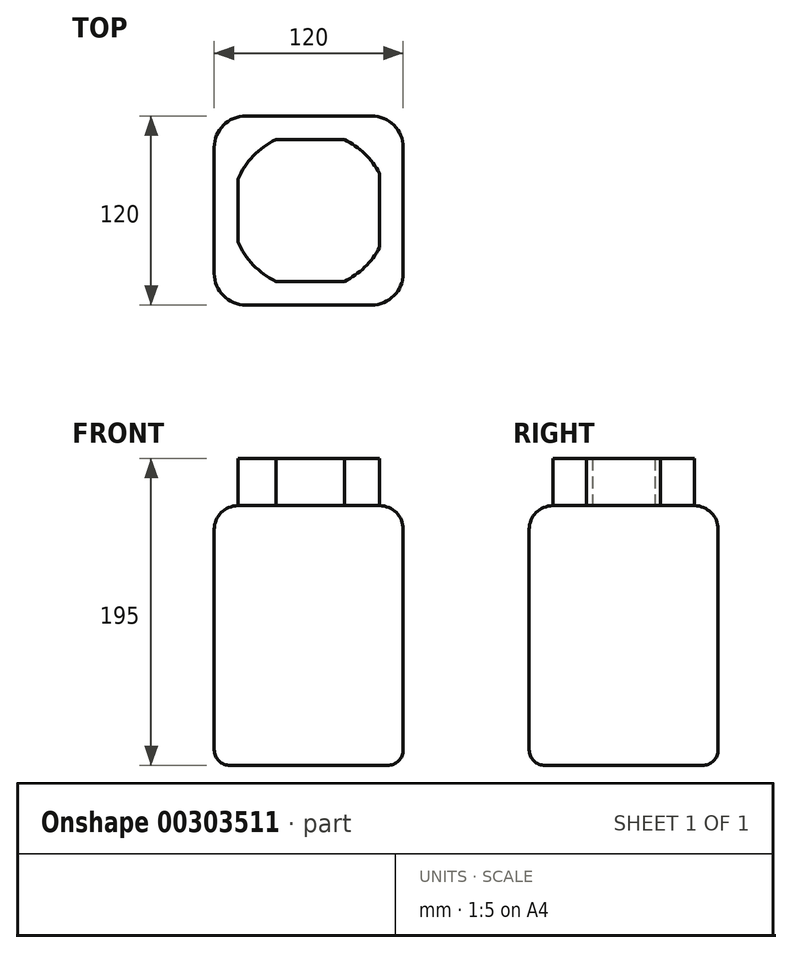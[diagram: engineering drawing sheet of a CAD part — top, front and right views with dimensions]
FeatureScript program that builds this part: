
annotation { "Feature Type Name" : "Feature", "Feature Type Description" : "" }
export const myFeature = defineFeature(function(context is Context, id is Id, definition is map)
    precondition{}
    {
        {
            var Q0;
            Q0=qCreatedBy(makeId("Top.planeOp"),FACE);
            var sketch = newSketch(context, id + "F0", { "sketchPlane" : qUnion([Q0])});
            skLineSegment(sketch, "E0.bottom", {"start": v(-100, 60) * mm, "end": v(-20, 60) * mm});
            skLineSegment(sketch, "E0.top", {"start": v(-100, -60) * mm, "end": v(-20, -60) * mm});
            skLineSegment(sketch, "E0.left", {"start": v(-120, 40) * mm, "end": v(-120, -40) * mm});
            skLineSegment(sketch, "E0.right", {"start": v(0, 40) * mm, "end": v(0, -40) * mm});
            skPoint(sketch, "E1.visualSharp", {"position": v(0, 60) * mm});
            skArc(sketch, "E1.filletArc", {"start": v(0, 40) * mm, "mid": v(-5.86, 54.14) * mm, "end": v(-20, 60) * mm});
            skPoint(sketch, "E2.visualSharp", {"position": v(0, -60) * mm});
            skArc(sketch, "E2.filletArc", {"start": v(-20, -60) * mm, "mid": v(-5.86, -54.14) * mm, "end": v(0, -40) * mm});
            skPoint(sketch, "E3.visualSharp", {"position": v(-120, -60) * mm});
            skArc(sketch, "E3.filletArc", {"start": v(-120, -40) * mm, "mid": v(-114.14, -54.14) * mm, "end": v(-100, -60) * mm});
            skPoint(sketch, "E4.visualSharp", {"position": v(-120, 60) * mm});
            skArc(sketch, "E4.filletArc", {"start": v(-100, 60) * mm, "mid": v(-114.14, 54.14) * mm, "end": v(-120, 40) * mm});
            skSolve(sketch);
        }
        {
            var Q0;
            Q0=makeQuery(id+"F0.imprint","IMPRINT",FACE,{"disambiguationData":[TD([[makeQuery(id+"F0.imprint","IMPRINT",EDGE,{"derivedFrom":sQuery(id+"F0.wireOp",EDGE,"E0.bottom")}),-1.0]])]});
            extrude(context, id + "F1", {"entities" : qUnion([Q0]), "depth" : 165 * mm});
        }
        {
            var Q0;
            Q0=makeQuery(id+"F1.opExtrude","CAP_EDGE",EDGE,{"disambiguationData":[OSD([sQuery(id+"F0.wireOp",EDGE,"E0.top")])],"isStart":true});
            var Q1;
            Q1=makeQuery(id+"F1.opExtrude","CAP_EDGE",EDGE,{"disambiguationData":[OSD([sQuery(id+"F0.wireOp",EDGE,"E3.filletArc")])],"isStart":true});
            var Q2;
            Q2=makeQuery(id+"F1.opExtrude","CAP_EDGE",EDGE,{"disambiguationData":[OSD([sQuery(id+"F0.wireOp",EDGE,"E2.filletArc")])],"isStart":true});
            fillet(context, id + "F2", {"entities" : qUnion([Q0, Q1, Q2]), "radius" : 10 * mm, "tangentPropagation" : true, "allowEdgeOverflow" : false});
        }
        {
            var Q0;
            Q0=makeQuery(id+"F1.opExtrude","CAP_EDGE",EDGE,{"disambiguationData":[OSD([sQuery(id+"F0.wireOp",EDGE,"E0.bottom")])],"isStart":false});
            fillet(context, id + "F3", {"entities" : qUnion([Q0]), "radius" : 15 * mm, "tangentPropagation" : true, "allowEdgeOverflow" : false});
        }
        {
            var Q0;
            Q0=makeQuery(id+"F1.opExtrude","CAP_FACE",FACE,{"disambiguationData":[OSD([sQuery(id+"F0.wireOp",EDGE,"E0.bottom"),sQuery(id+"F0.wireOp",EDGE,"E0.top"),sQuery(id+"F0.wireOp",EDGE,"E0.left"),sQuery(id+"F0.wireOp",EDGE,"E0.right"),sQuery(id+"F0.wireOp",EDGE,"E1.filletArc"),sQuery(id+"F0.wireOp",EDGE,"E2.filletArc"),sQuery(id+"F0.wireOp",EDGE,"E3.filletArc"),sQuery(id+"F0.wireOp",EDGE,"E4.filletArc")])],"isStart":false});
            var sketch = newSketch(context, id + "F4", { "sketchPlane" : qUnion([Q0])});
            skCircle(sketch, "E5", {"center": v(-59.14, 0) * mm, "radius": 50 * mm});
            skSolve(sketch);
        }
        {
            var Q0;
            {var subQ0=sQuery(id+"F4.wireOp",EDGE,"E5");var subQ1=sQuery(id+"F0.wireOp",EDGE,"E0.right");var subQ2=sQuery(id+"F0.wireOp",EDGE,"E0.left");var subQ3=sQuery(id+"F0.wireOp",EDGE,"E0.top");var subQ4=sQuery(id+"F0.wireOp",EDGE,"E0.bottom");var subQ5=makeQuery(id+"F1.opExtrude","CAP_FACE",FACE,{"disambiguationData":[OSD([subQ4,subQ3,subQ2,subQ1,sQuery(id+"F0.wireOp",EDGE,"E1.filletArc"),sQuery(id+"F0.wireOp",EDGE,"E2.filletArc"),sQuery(id+"F0.wireOp",EDGE,"E3.filletArc"),sQuery(id+"F0.wireOp",EDGE,"E4.filletArc")])],"isStart":false});var subQ13=makeQuery(id+"F3.opFillet","BLEND_EDGE",EDGE,{"blendedFrom":[makeQuery(id+"F1.opExtrude","CAP_EDGE",EDGE,{"disambiguationData":[OSD([subQ4])],"isStart":false}),subQ5],"blendedInto":[subQ5]});var subQ16=makeQuery(id+"F4.imprint","INTERSECT",VERTEX,{"disambiguationData":[OD(0.0)],"derivedFrom":[subQ13,subQ0]});Q0=makeQuery(id+"F4.imprint","IMPRINT",FACE,{"disambiguationData":[TD([[makeQuery(id+"F4.imprint","IMPRINT",EDGE,{"disambiguationData":[TD([[subQ16,1.0]])],"derivedFrom":subQ0}),1.0]])]});}
            extrude(context, id + "F5", {"entities" : qUnion([Q0]), "operationType" : NewBodyOperationType.ADD, "depth" : 30 * mm});
        }
    });
